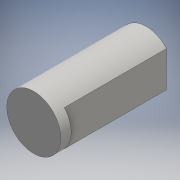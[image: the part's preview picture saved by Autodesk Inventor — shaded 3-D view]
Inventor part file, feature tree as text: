
AUTODESK INVENTOR PART (.ipt)
format: ipt  version: 2016 (Build 200138000, 138)  size: 97,280 bytes
history: native  units: mm
features: extrude x2, sketch x2, other x1
ambient origin geometry x8: Origin, YZ Plane, XZ Plane, XY Plane, X Axis, Y Axis, Z Axis, Center Point
bodies: Body1 (feature_tree)
feature tree (5):
  other  "ソリッド1"
  extrude  "押し出し1"  Depth=12.0mm
  extrude  "押し出し3"  Depth=25.0mm TaperAngle=0.0deg
  sketch  "スケッチ1"
  sketch  "スケッチ4"
